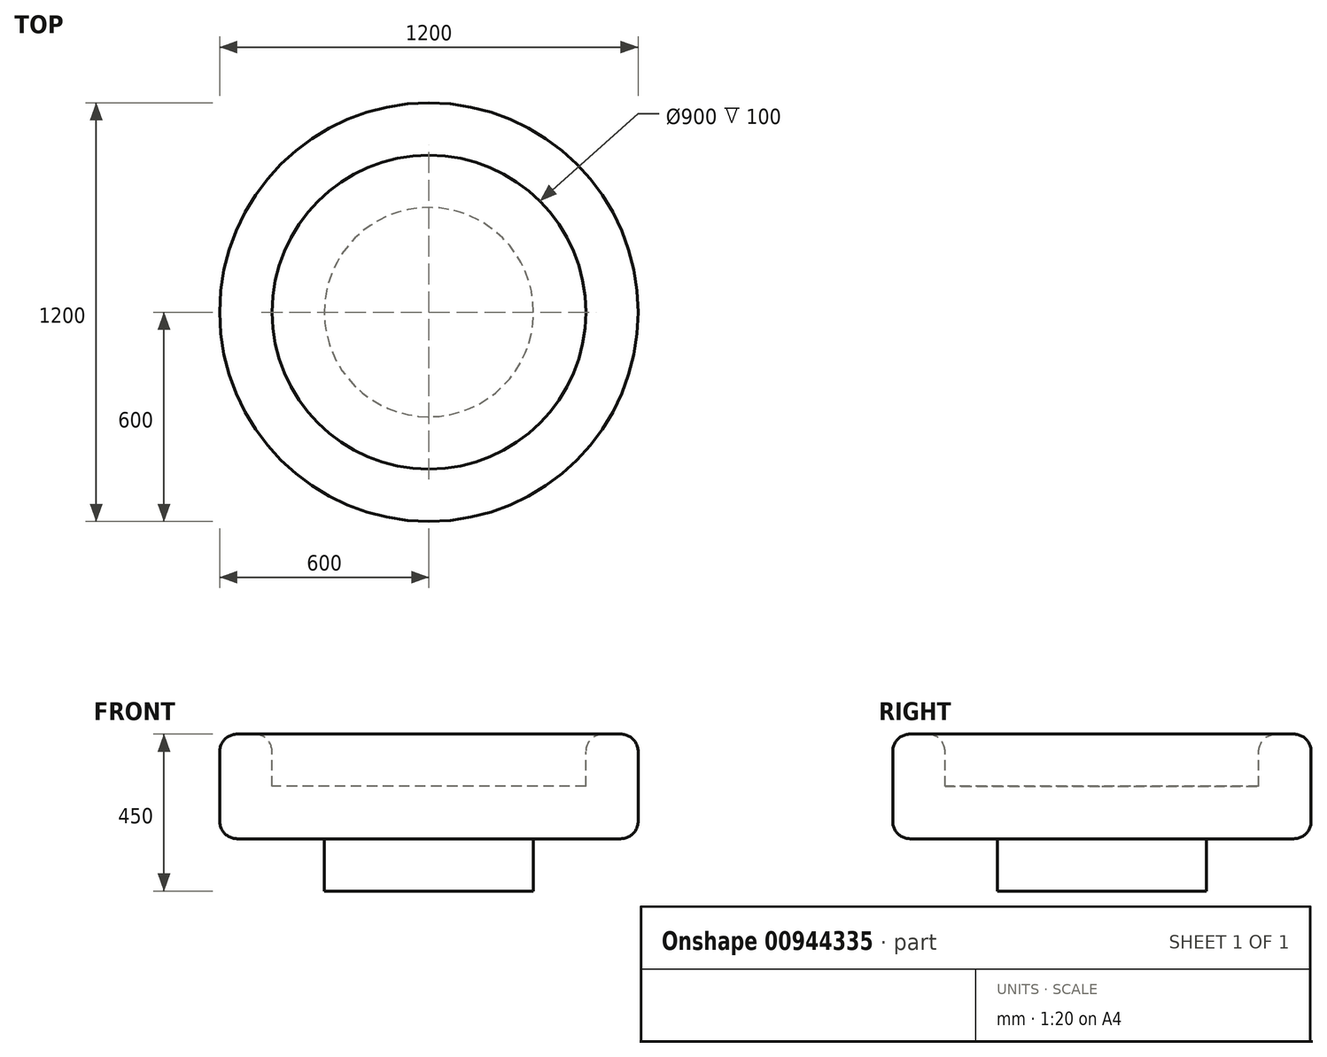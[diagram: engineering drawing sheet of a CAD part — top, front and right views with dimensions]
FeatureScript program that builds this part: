
annotation { "Feature Type Name" : "Feature", "Feature Type Description" : "" }
export const myFeature = defineFeature(function(context is Context, id is Id, definition is map)
    precondition{}
    {
        {
            var Q0;
            Q0=qCreatedBy(makeId("Front.planeOp"),FACE);
            var sketch = newSketch(context, id + "F0", { "sketchPlane" : qUnion([Q0])});
            skLineSegment(sketch, "E0", {"start": v(0, 54.44) * mm, "end": v(0, -35.03) * mm});
            skLineSegment(sketch, "E1", {"start": v(0, 0) * mm, "end": v(-450, 0) * mm});
            skLineSegment(sketch, "E2", {"start": v(-450, 0) * mm, "end": v(-450, 150) * mm});
            skLineSegment(sketch, "E3", {"start": v(-450, 150) * mm, "end": v(-600, 150) * mm});
            skLineSegment(sketch, "E4", {"start": v(-600, 150) * mm, "end": v(-600, -150) * mm});
            skLineSegment(sketch, "E5", {"start": v(-600, -150) * mm, "end": v(-300, -150) * mm});
            skLineSegment(sketch, "E6", {"start": v(-300, -150) * mm, "end": v(-300, -300) * mm});
            skLineSegment(sketch, "E7", {"start": v(-300, -300) * mm, "end": v(0, -300) * mm});
            skLineSegment(sketch, "E8", {"start": v(0, -300) * mm, "end": v(0, 0) * mm});
            skSolve(sketch);
        }
        {
            var Q0;
            Q0=makeQuery(id+"F0.imprint","IMPRINT",FACE,{"disambiguationData":[TD([[makeQuery(id+"F0.imprint","IMPRINT",EDGE,{"derivedFrom":sQuery(id+"F0.wireOp",EDGE,"E1")}),1.0]])]});
            var Q1;
            Q1=sQuery(id+"F0.wireOp",EDGE,"E0");
            revolve(context, id + "F1", {"surfaceOperationType" : NewSurfaceOperationType.NEW, "entities" : qUnion([Q0]), "axis" : qUnion([Q1]), "revolveType" : RevolveType.FULL});
        }
        {
            var Q0;
            Q0=makeQuery(id+"F1.opRevolve","SWEPT_EDGE",EDGE,{"disambiguationData":[OSD([sQuery(id+"F0.wireOp",EDGE,"E3"),sQuery(id+"F0.wireOp",EDGE,"E4")])]});
            var Q1;
            Q1=makeQuery(id+"F1.opRevolve","SWEPT_EDGE",EDGE,{"disambiguationData":[OSD([sQuery(id+"F0.wireOp",EDGE,"E2"),sQuery(id+"F0.wireOp",EDGE,"E3")])]});
            var Q2;
            Q2=makeQuery(id+"F1.opRevolve","SWEPT_EDGE",EDGE,{"disambiguationData":[OSD([sQuery(id+"F0.wireOp",EDGE,"E4"),sQuery(id+"F0.wireOp",EDGE,"E5")])]});
            fillet(context, id + "F2", {"entities" : qUnion([Q0, Q1, Q2]), "radius" : 50 * mm, "tangentPropagation" : true, "allowEdgeOverflow" : false});
        }
    });
